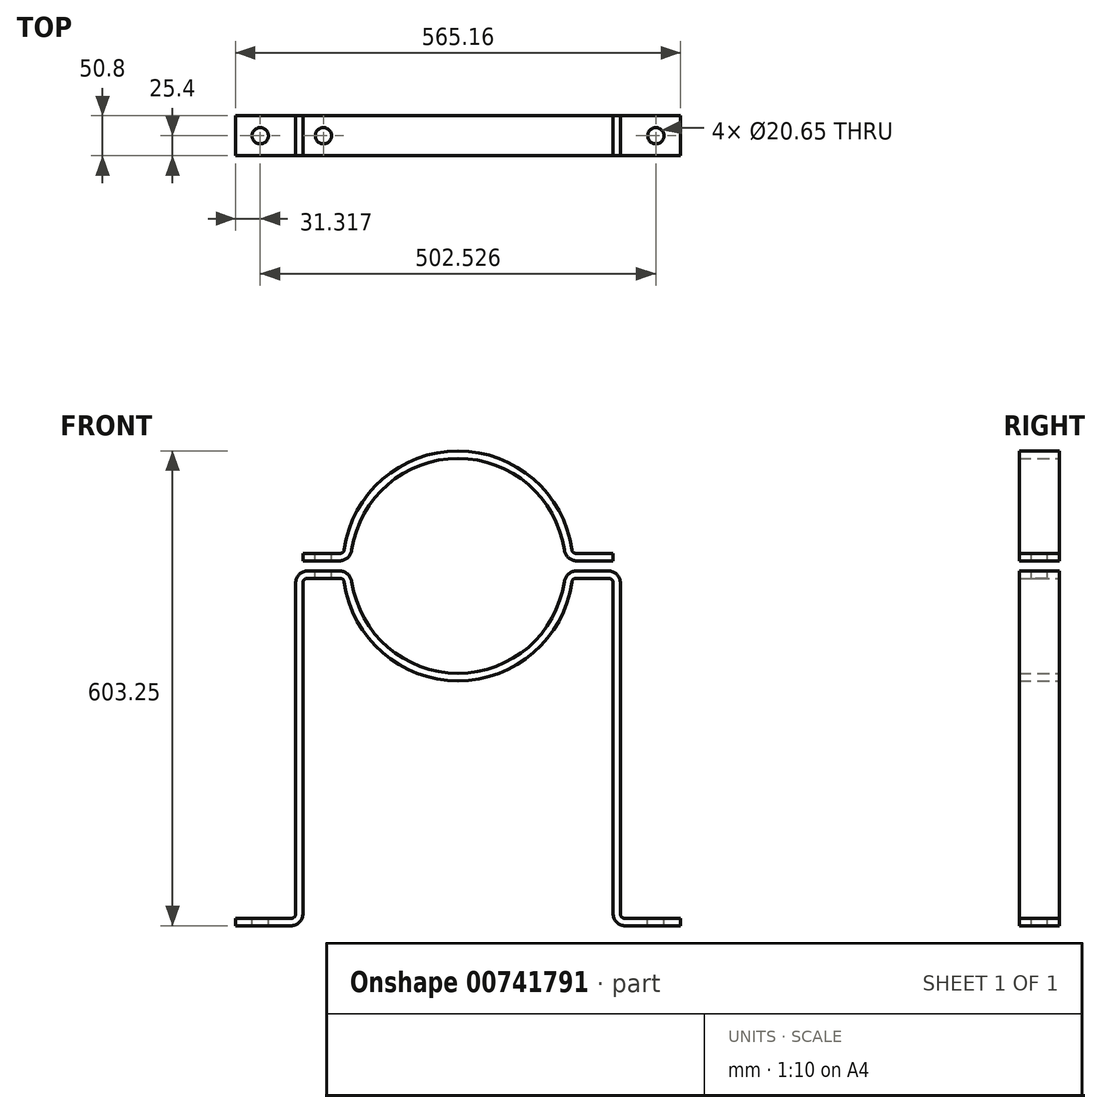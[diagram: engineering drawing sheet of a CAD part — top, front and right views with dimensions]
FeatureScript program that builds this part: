
annotation { "Feature Type Name" : "Feature", "Feature Type Description" : "" }
export const myFeature = defineFeature(function(context is Context, id is Id, definition is map)
    precondition{}
    {
        {
            var Q0;
            Q0=qCreatedBy(makeId("Front.planeOp"),FACE);
            var sketch = newSketch(context, id + "F0", { "sketchPlane" : qUnion([Q0])});
            skArc(sketch, "E0", {"start": v(136.38, 6.35) * mm, "mid": v(-136.53, 0) * mm, "end": v(136.38, -6.35) * mm});
            skLineSegment(sketch, "E1.bottom", {"start": v(196.85, 6.35) * mm, "end": v(136.38, 6.35) * mm});
            skLineSegment(sketch, "E1.top", {"start": v(196.85, 15.87) * mm, "end": v(145.18, 15.87) * mm});
            skLineSegment(sketch, "E1.left", {"start": v(196.85, 6.35) * mm, "end": v(196.85, 15.87) * mm});
            skLineSegment(sketch, "E1.right", {"start": v(-196.85, 6.35) * mm, "end": v(-196.85, 15.88) * mm});
            skPoint(sketch, "E1.middle", {"position": v(0, 11.11) * mm});
            skLineSegment(sketch, "E2.MirrorCS", {"start": v(196.85, -6.35) * mm, "end": v(136.38, -6.35) * mm});
            skLineSegment(sketch, "E3.MirrorCS", {"start": v(196.85, -15.87) * mm, "end": v(145.18, -15.87) * mm});
            skLineSegment(sketch, "E4.MirrorCS", {"start": v(196.85, -6.35) * mm, "end": v(196.85, -15.87) * mm});
            skLineSegment(sketch, "E5", {"start": v(0, 0) * mm, "end": v(0, -457.2) * mm});
            skPoint(sketch, "E5.endSnap0", {"position": v(0, -15.88) * mm});
            skLineSegment(sketch, "E6", {"start": v(-196.85, -15.88) * mm, "end": v(-196.85, -457.2) * mm});
            skLineSegment(sketch, "E7", {"start": v(-196.85, -457.2) * mm, "end": v(-282.57, -457.2) * mm});
            skLineSegment(sketch, "E8", {"start": v(-282.57, -457.2) * mm, "end": v(-282.57, -447.68) * mm});
            skLineSegment(sketch, "E9", {"start": v(-282.57, -447.68) * mm, "end": v(-206.37, -447.68) * mm});
            skLineSegment(sketch, "E10", {"start": v(-206.37, -447.68) * mm, "end": v(-206.37, -6.35) * mm});
            skLineSegment(sketch, "E11", {"start": v(-206.37, -6.35) * mm, "end": v(-196.85, -6.35) * mm});
            skLineSegment(sketch, "E12.MirrorCS", {"start": v(196.85, -15.88) * mm, "end": v(196.85, -457.2) * mm});
            skLineSegment(sketch, "E13.MirrorCS", {"start": v(206.37, -447.68) * mm, "end": v(206.37, -6.35) * mm});
            skLineSegment(sketch, "E14.MirrorCS", {"start": v(206.37, -6.35) * mm, "end": v(196.85, -6.35) * mm});
            skLineSegment(sketch, "E15.MirrorCS", {"start": v(282.57, -447.67) * mm, "end": v(206.37, -447.67) * mm});
            skLineSegment(sketch, "E16.MirrorCS", {"start": v(196.85, -457.2) * mm, "end": v(282.57, -457.2) * mm});
            skLineSegment(sketch, "E17.MirrorCS", {"start": v(282.57, -457.2) * mm, "end": v(282.57, -447.68) * mm});
            skLineSegment(sketch, "E18.trimOffspring", {"start": v(-145.18, 15.88) * mm, "end": v(-196.85, 15.88) * mm});
            skLineSegment(sketch, "E19.trimOffspring", {"start": v(-136.38, 6.35) * mm, "end": v(-196.85, 6.35) * mm});
            skArc(sketch, "E20.trimOffspring", {"start": v(-145.18, -15.87) * mm, "mid": v(0, -146.05) * mm, "end": v(145.18, -15.87) * mm});
            skLineSegment(sketch, "E21.trimOffspring", {"start": v(-145.18, -15.88) * mm, "end": v(-196.85, -15.88) * mm});
            skPoint(sketch, "E22.MirrorCS.end.orphan", {"position": v(-196.85, -15.88) * mm});
            skLineSegment(sketch, "E23.trimOffspring", {"start": v(-136.38, -6.35) * mm, "end": v(-196.85, -6.35) * mm});
            skArc(sketch, "E24.trimOffspring", {"start": v(145.18, 15.87) * mm, "mid": v(0, 146.05) * mm, "end": v(-145.18, 15.88) * mm});
            skSolve(sketch);
        }
        {
            var Q0;
            Q0 = qSketchRegion(id + "F0", true);
            extrude(context, id + "F1", {"entities" : qUnion([Q0]), "endBound" : BoundingType.SYMMETRIC, "depth" : 50.8 * mm, "offsetDistance" : 25.4 * mm});
        }
        {
            var Q0;
            Q0=makeQuery(id+"F1.opExtrude","SWEPT_FACE",FACE,{"disambiguationData":[OSD([sQuery(id+"F0.wireOp",EDGE,"E18.trimOffspring")])]});
            var sketch = newSketch(context, id + "F2", { "sketchPlane" : qUnion([Q0])});
            skCircle(sketch, "E25", {"center": v(-171.02, 0) * mm, "radius": 10.33 * mm});
            skPoint(sketch, "E25.centerSnap0", {"position": v(-171.02, -25.4) * mm});
            skCircle(sketch, "E26.MirrorC", {"center": v(171.02, 0) * mm, "radius": 10.33 * mm});
            skSolve(sketch);
        }
        {
            var Q0;
            Q0=makeQuery(id+"F2.imprint","IMPRINT",FACE,{"disambiguationData":[TD([[makeQuery(id+"F2.imprint","IMPRINT",EDGE,{"derivedFrom":sQuery(id+"F2.wireOp",EDGE,"E25")}),1.0]])]});
            var Q1;
            Q1=makeQuery(id+"F2.imprint","IMPRINT",FACE,{"disambiguationData":[TD([[makeQuery(id+"F2.imprint","IMPRINT",EDGE,{"derivedFrom":sQuery(id+"F2.wireOp",EDGE,"E26.MirrorC")}),-1.0]])]});
            extrude(context, id + "F3", {"entities" : qUnion([Q0, Q1]), "operationType" : NewBodyOperationType.REMOVE, "endBound" : BoundingType.THROUGH_ALL, "oppositeDirection" : true, "depth" : 50.8 * mm, "offsetDistance" : 25.4 * mm});
        }
        {
            var Q0;
            Q0=makeQuery(id+"F1.opExtrude","SWEPT_FACE",FACE,{"disambiguationData":[OSD([sQuery(id+"F0.wireOp",EDGE,"E9")])]});
            var sketch = newSketch(context, id + "F4", { "sketchPlane" : qUnion([Q0])});
            skCircle(sketch, "E27", {"center": v(-251.26, 0) * mm, "radius": 10.33 * mm});
            skPoint(sketch, "E27.centerSnap0", {"position": v(-282.57, 0) * mm});
            skCircle(sketch, "E28.MirrorC", {"center": v(251.26, 0) * mm, "radius": 10.33 * mm});
            skSolve(sketch);
        }
        {
            var Q0;
            Q0 = qSketchRegion(id + "F4", true);
            extrude(context, id + "F5", {"entities" : qUnion([Q0]), "operationType" : NewBodyOperationType.REMOVE, "oppositeDirection" : true, "depth" : 25.4 * mm, "offsetDistance" : 25.4 * mm});
        }
        {
            var Q0;
            Q0=makeQuery(id+"F1.opExtrude","SWEPT_EDGE",EDGE,{"disambiguationData":[OSD([sQuery(id+"F0.wireOp",EDGE,"E9"),sQuery(id+"F0.wireOp",EDGE,"E10")])]});
            var Q1;
            Q1=makeQuery(id+"F1.opExtrude","SWEPT_EDGE",EDGE,{"disambiguationData":[OSD([sQuery(id+"F0.wireOp",EDGE,"E18.trimOffspring"),sQuery(id+"F0.wireOp",EDGE,"E24.trimOffspring")])]});
            var Q2;
            Q2=makeQuery(id+"F1.opExtrude","SWEPT_EDGE",EDGE,{"disambiguationData":[OSD([sQuery(id+"F0.wireOp",EDGE,"E1.top"),sQuery(id+"F0.wireOp",EDGE,"E24.trimOffspring")])]});
            var Q3;
            Q3=makeQuery(id+"F1.opExtrude","SWEPT_EDGE",EDGE,{"disambiguationData":[OSD([sQuery(id+"F0.wireOp",EDGE,"E13.MirrorCS"),sQuery(id+"F0.wireOp",EDGE,"E15.MirrorCS")])]});
            var Q4;
            Q4=makeQuery(id+"F1.opExtrude","SWEPT_EDGE",EDGE,{"disambiguationData":[OSD([sQuery(id+"F0.wireOp",EDGE,"E3.MirrorCS"),sQuery(id+"F0.wireOp",EDGE,"E4.MirrorCS"),sQuery(id+"F0.wireOp",EDGE,"E12.MirrorCS")])]});
            var Q5;
            Q5=makeQuery(id+"F1.opExtrude","SWEPT_EDGE",EDGE,{"disambiguationData":[OSD([sQuery(id+"F0.wireOp",EDGE,"E3.MirrorCS"),sQuery(id+"F0.wireOp",EDGE,"E20.trimOffspring")])]});
            var Q6;
            Q6=makeQuery(id+"F1.opExtrude","SWEPT_EDGE",EDGE,{"disambiguationData":[OSD([sQuery(id+"F0.wireOp",EDGE,"E6"),sQuery(id+"F0.wireOp",EDGE,"E21.trimOffspring")])]});
            var Q7;
            Q7=makeQuery(id+"F1.opExtrude","SWEPT_EDGE",EDGE,{"disambiguationData":[OSD([sQuery(id+"F0.wireOp",EDGE,"E20.trimOffspring"),sQuery(id+"F0.wireOp",EDGE,"E21.trimOffspring")])]});
            fillet(context, id + "F6", {"entities" : qUnion([Q0, Q1, Q2, Q3, Q4, Q5, Q6, Q7]), "radius" : 5.08 * mm, "tangentPropagation" : true, "allowEdgeOverflow" : false});
        }
        {
            var Q0;
            Q0=makeQuery(id+"F1.opExtrude","SWEPT_EDGE",EDGE,{"disambiguationData":[OSD([sQuery(id+"F0.wireOp",EDGE,"E0"),sQuery(id+"F0.wireOp",EDGE,"E23.trimOffspring")])]});
            var Q1;
            Q1=makeQuery(id+"F1.opExtrude","SWEPT_EDGE",EDGE,{"disambiguationData":[OSD([sQuery(id+"F0.wireOp",EDGE,"E10"),sQuery(id+"F0.wireOp",EDGE,"E11")])]});
            var Q2;
            Q2=makeQuery(id+"F1.opExtrude","SWEPT_EDGE",EDGE,{"disambiguationData":[OSD([sQuery(id+"F0.wireOp",EDGE,"E0"),sQuery(id+"F0.wireOp",EDGE,"E19.trimOffspring")])]});
            var Q3;
            Q3=makeQuery(id+"F1.opExtrude","SWEPT_EDGE",EDGE,{"disambiguationData":[OSD([sQuery(id+"F0.wireOp",EDGE,"E13.MirrorCS"),sQuery(id+"F0.wireOp",EDGE,"E14.MirrorCS")])]});
            var Q4;
            Q4=makeQuery(id+"F1.opExtrude","SWEPT_EDGE",EDGE,{"disambiguationData":[OSD([sQuery(id+"F0.wireOp",EDGE,"E0"),sQuery(id+"F0.wireOp",EDGE,"E2.MirrorCS")])]});
            var Q5;
            Q5=makeQuery(id+"F1.opExtrude","SWEPT_EDGE",EDGE,{"disambiguationData":[OSD([sQuery(id+"F0.wireOp",EDGE,"E0"),sQuery(id+"F0.wireOp",EDGE,"E1.bottom")])]});
            var Q6;
            Q6=makeQuery(id+"F1.opExtrude","SWEPT_EDGE",EDGE,{"disambiguationData":[OSD([sQuery(id+"F0.wireOp",EDGE,"E6"),sQuery(id+"F0.wireOp",EDGE,"E7")])]});
            var Q7;
            Q7=makeQuery(id+"F1.opExtrude","SWEPT_EDGE",EDGE,{"disambiguationData":[OSD([sQuery(id+"F0.wireOp",EDGE,"E12.MirrorCS"),sQuery(id+"F0.wireOp",EDGE,"E16.MirrorCS")])]});
            fillet(context, id + "F7", {"entities" : qUnion([Q0, Q1, Q2, Q3, Q4, Q5, Q6, Q7]), "radius" : 15.88 * mm, "tangentPropagation" : true, "allowEdgeOverflow" : false});
        }
    });
